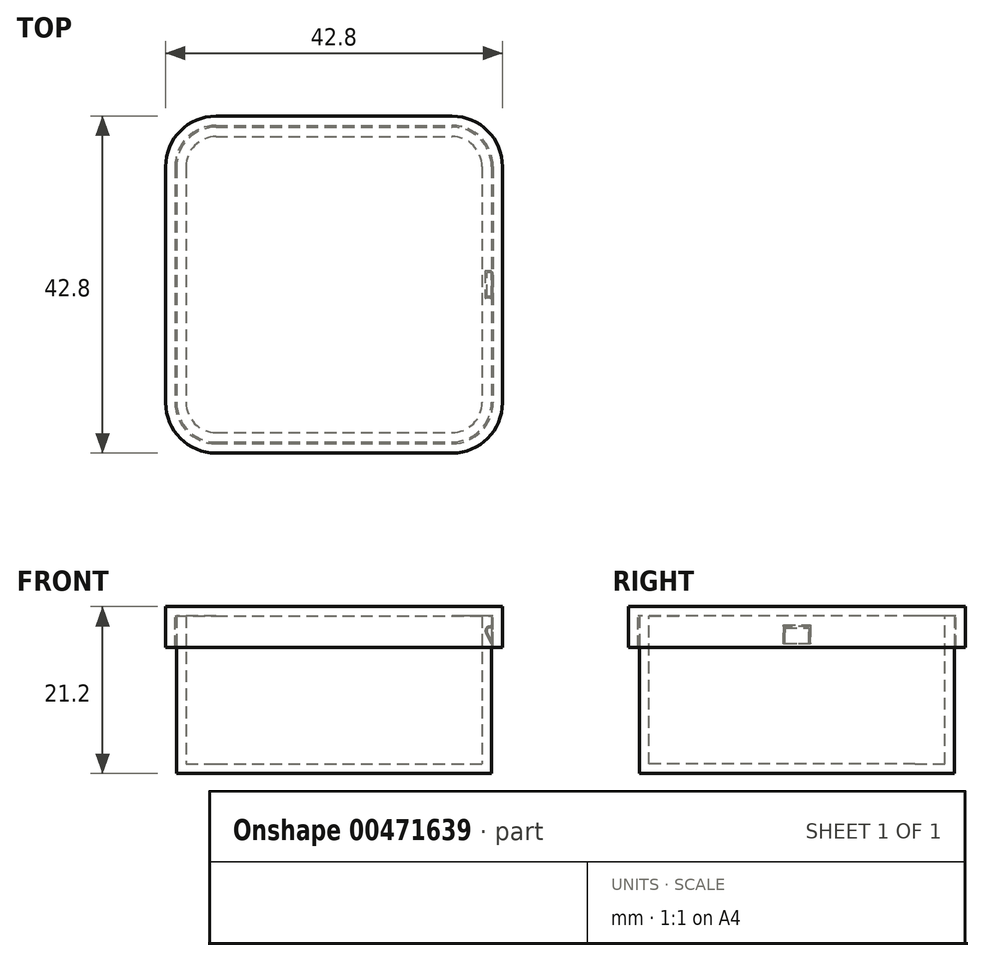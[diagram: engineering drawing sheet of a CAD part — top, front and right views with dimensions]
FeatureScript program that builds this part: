
annotation { "Feature Type Name" : "Feature", "Feature Type Description" : "" }
export const myFeature = defineFeature(function(context is Context, id is Id, definition is map)
    precondition{}
    {
        {
            var Q0;
            Q0=qCreatedBy(makeId("Top.planeOp"),FACE);
            var sketch = newSketch(context, id + "F0", { "sketchPlane" : qUnion([Q0])});
            skLineSegment(sketch, "E0.bottom", {"start": v(-20, 20) * mm, "end": v(20, 20) * mm});
            skLineSegment(sketch, "E0.top", {"start": v(-20, -20) * mm, "end": v(20, -20) * mm});
            skLineSegment(sketch, "E0.left", {"start": v(-20, 20) * mm, "end": v(-20, -20) * mm});
            skLineSegment(sketch, "E0.right", {"start": v(20, 20) * mm, "end": v(20, -20) * mm});
            skPoint(sketch, "E0.middle", {"position": v(0, 0) * mm});
            skSolve(sketch);
        }
        {
            var Q0;
            Q0 = qSketchRegion(id + "F0", true);
            extrude(context, id + "F1", {"entities" : qUnion([Q0]), "depth" : 20 * mm});
        }
        {
            var Q0;
            Q0=makeQuery(id+"F1.opExtrude","SWEPT_EDGE",EDGE,{"disambiguationData":[OSD([sQuery(id+"F0.wireOp",EDGE,"E0.top"),sQuery(id+"F0.wireOp",EDGE,"E0.right")])]});
            var Q1;
            Q1=makeQuery(id+"F1.opExtrude","SWEPT_EDGE",EDGE,{"disambiguationData":[OSD([sQuery(id+"F0.wireOp",EDGE,"E0.bottom"),sQuery(id+"F0.wireOp",EDGE,"E0.right")])]});
            var Q2;
            Q2=makeQuery(id+"F1.opExtrude","SWEPT_EDGE",EDGE,{"disambiguationData":[OSD([sQuery(id+"F0.wireOp",EDGE,"E0.top"),sQuery(id+"F0.wireOp",EDGE,"E0.left")])]});
            var Q3;
            Q3=makeQuery(id+"F1.opExtrude","SWEPT_EDGE",EDGE,{"disambiguationData":[OSD([sQuery(id+"F0.wireOp",EDGE,"E0.bottom"),sQuery(id+"F0.wireOp",EDGE,"E0.left")])]});
            fillet(context, id + "F2", {"entities" : qUnion([Q0, Q1, Q2, Q3]), "radius" : 5 * mm, "tangentPropagation" : true, "allowEdgeOverflow" : false});
        }
        {
            var Q0;
            Q0=makeQuery(id+"F1.opExtrude","CAP_FACE",FACE,{"disambiguationData":[OSD([sQuery(id+"F0.wireOp",EDGE,"E0.bottom"),sQuery(id+"F0.wireOp",EDGE,"E0.top"),sQuery(id+"F0.wireOp",EDGE,"E0.left"),sQuery(id+"F0.wireOp",EDGE,"E0.right")])],"isStart":false});
            shell(context, id + "F3", {"entities" : qUnion([Q0]), "thickness" : 1.2 * mm});
        }
        {
            var Q0;
            Q0=makeQuery(id+"F1.opExtrude","CAP_FACE",FACE,{"disambiguationData":[OSD([sQuery(id+"F0.wireOp",EDGE,"E0.bottom"),sQuery(id+"F0.wireOp",EDGE,"E0.top"),sQuery(id+"F0.wireOp",EDGE,"E0.left"),sQuery(id+"F0.wireOp",EDGE,"E0.right")])],"isStart":false});
            var sketch = newSketch(context, id + "F4", { "sketchPlane" : qUnion([Q0])});
            skLineSegment(sketch, "E1.0", {"start": v(-15, -20) * mm, "end": v(15, -20) * mm});
            skArc(sketch, "E1.1", {"start": v(15, -20) * mm, "mid": v(18.54, -18.54) * mm, "end": v(20, -15) * mm});
            skLineSegment(sketch, "E1.2", {"start": v(20, 15) * mm, "end": v(20, -15) * mm});
            skArc(sketch, "E1.3", {"start": v(20, 15) * mm, "mid": v(18.54, 18.54) * mm, "end": v(15, 20) * mm});
            skLineSegment(sketch, "E1.4", {"start": v(-15, 20) * mm, "end": v(15, 20) * mm});
            skArc(sketch, "E1.5", {"start": v(-15, 20) * mm, "mid": v(-18.54, 18.54) * mm, "end": v(-20, 15) * mm});
            skLineSegment(sketch, "E1.6", {"start": v(-20, 15) * mm, "end": v(-20, -15) * mm});
            skArc(sketch, "E1.7", {"start": v(-20, -15) * mm, "mid": v(-18.54, -18.54) * mm, "end": v(-15, -20) * mm});
            skArc(sketch, "E2.0", {"start": v(-20.2, -15) * mm, "mid": v(-18.68, -18.68) * mm, "end": v(-15, -20.2) * mm});
            skLineSegment(sketch, "E2.1", {"start": v(-20.2, 15) * mm, "end": v(-20.2, -15) * mm});
            skLineSegment(sketch, "E2.2", {"start": v(-15, -20.2) * mm, "end": v(15, -20.2) * mm});
            skArc(sketch, "E2.3", {"start": v(-15, 20.2) * mm, "mid": v(-18.68, 18.68) * mm, "end": v(-20.2, 15) * mm});
            skArc(sketch, "E2.4", {"start": v(15, -20.2) * mm, "mid": v(18.68, -18.68) * mm, "end": v(20.2, -15) * mm});
            skLineSegment(sketch, "E2.5", {"start": v(20.2, 15) * mm, "end": v(20.2, -15) * mm});
            skArc(sketch, "E2.6", {"start": v(20.2, 15) * mm, "mid": v(18.68, 18.68) * mm, "end": v(15, 20.2) * mm});
            skLineSegment(sketch, "E2.7", {"start": v(-15, 20.2) * mm, "end": v(15, 20.2) * mm});
            skArc(sketch, "E3.0", {"start": v(-21.4, -15) * mm, "mid": v(-19.53, -19.53) * mm, "end": v(-15, -21.4) * mm});
            skLineSegment(sketch, "E3.1", {"start": v(-21.4, 15) * mm, "end": v(-21.4, -15) * mm});
            skLineSegment(sketch, "E3.2", {"start": v(-15, -21.4) * mm, "end": v(15, -21.4) * mm});
            skArc(sketch, "E3.3", {"start": v(-15, 21.4) * mm, "mid": v(-19.53, 19.53) * mm, "end": v(-21.4, 15) * mm});
            skArc(sketch, "E3.4", {"start": v(15, -21.4) * mm, "mid": v(19.53, -19.53) * mm, "end": v(21.4, -15) * mm});
            skLineSegment(sketch, "E3.5", {"start": v(21.4, 15) * mm, "end": v(21.4, -15) * mm});
            skArc(sketch, "E3.6", {"start": v(21.4, 15) * mm, "mid": v(19.53, 19.53) * mm, "end": v(15, 21.4) * mm});
            skLineSegment(sketch, "E3.7", {"start": v(-15, 21.4) * mm, "end": v(15, 21.4) * mm});
            skSolve(sketch);
        }
        {
            var Q0;
            Q0=makeQuery(id+"F4.imprint","IMPRINT",FACE,{"disambiguationData":[TD([[makeQuery(id+"F4.imprint","IMPRINT",EDGE,{"derivedFrom":sQuery(id+"F4.wireOp",EDGE,"E2.0")}),-1.0]])]});
            var Q1;
            {var subQ3=sQuery(id+"F0.wireOp",EDGE,"E0.bottom");Q1=makeQuery(id+"F4.imprint","IMPRINT",FACE,{"disambiguationData":[TD([[makeQuery(id+"F4.imprint","IMPRINT",EDGE,{"derivedFrom":makeQuery(id+"F3.opShell","OFFSET_EDGE",EDGE,{"disambiguationData":[OSD([subQ3]),TDD([makeQuery(id+"F1.opExtrude","CAP_EDGE",EDGE,{"disambiguationData":[OSD([subQ3])],"isStart":false})])]})}),-1.0]])]});}
            var Q2;
            Q2=makeQuery(id+"F4.imprint","IMPRINT",FACE,{"disambiguationData":[TD([[makeQuery(id+"F4.imprint","IMPRINT",EDGE,{"derivedFrom":sQuery(id+"F4.wireOp",EDGE,"E1.0")}),1.0]])]});
            var Q3;
            Q3=makeQuery(id+"F4.imprint","IMPRINT",FACE,{"disambiguationData":[TD([[makeQuery(id+"F4.imprint","IMPRINT",EDGE,{"derivedFrom":sQuery(id+"F4.wireOp",EDGE,"E1.0")}),-1.0]])]});
            extrude(context, id + "F5", {"entities" : qUnion([Q0, Q1, Q2, Q3]), "depth" : 1.2 * mm});
        }
        {
            var Q0;
            Q0=makeQuery(id+"F4.imprint","IMPRINT",FACE,{"disambiguationData":[TD([[makeQuery(id+"F4.imprint","IMPRINT",EDGE,{"derivedFrom":sQuery(id+"F4.wireOp",EDGE,"E2.0")}),-1.0]])]});
            extrude(context, id + "F6", {"entities" : qUnion([Q0]), "operationType" : NewBodyOperationType.ADD, "oppositeDirection" : true, "depth" : 4 * mm});
        }
        {
            var Q0;
            Q0=qCreatedBy(makeId("Front.planeOp"),FACE);
            var sketch = newSketch(context, id + "F7", { "sketchPlane" : qUnion([Q0])});
            skLineSegment(sketch, "E4", {"start": v(20.2, 16.5) * mm, "end": v(20.2, 18.5) * mm});
            skLineSegment(sketch, "E5", {"start": v(20.2, 18.5) * mm, "end": v(19.8, 18.5) * mm});
            skLineSegment(sketch, "E6", {"start": v(20.2, 16.5) * mm, "end": v(19.45, 17.91) * mm});
            skArc(sketch, "E7", {"start": v(19.8, 18.5) * mm, "mid": v(19.46, 18.3) * mm, "end": v(19.45, 17.91) * mm});
            skArc(sketch, "E8", {"start": v(19.8, 18.5) * mm, "mid": v(20.08, 18.62) * mm, "end": v(20.2, 18.9) * mm});
            skLineSegment(sketch, "E9", {"start": v(20.2, 18.5) * mm, "end": v(19.4, 18.5) * mm, "construction": true});
            skLineSegment(sketch, "E10", {"start": v(20.2, 18.5) * mm, "end": v(20.2, 18.9) * mm});
            skArc(sketch, "E11.0", {"start": v(19.8, 18.7) * mm, "mid": v(19.92, 18.74) * mm, "end": v(19.99, 18.84) * mm});
            skArc(sketch, "E11.1", {"start": v(19.8, 18.7) * mm, "mid": v(19.29, 18.4) * mm, "end": v(19.27, 17.82) * mm});
            skLineSegment(sketch, "E11.2", {"start": v(20.2, 16.08) * mm, "end": v(19.27, 17.82) * mm});
            skLineSegment(sketch, "E12", {"start": v(19.99, 18.84) * mm, "end": v(20.2, 19.45) * mm});
            skLineSegment(sketch, "E13", {"start": v(20.2, 18.9) * mm, "end": v(20.2, 20) * mm});
            skLineSegment(sketch, "E14", {"start": v(20.2, 16.5) * mm, "end": v(20.2, 16.08) * mm});
            skLineSegment(sketch, "E15.0.1", {"start": v(20.2, 20) * mm, "end": v(20.2, 16) * mm, "construction": true});
            skLineSegment(sketch, "E15.0.3", {"start": v(20.2, 16) * mm, "end": v(20.2, 20) * mm, "construction": true});
            skLineSegment(sketch, "E16.0", {"start": v(20, 20) * mm, "end": v(20, 0) * mm, "construction": true});
            skSolve(sketch);
        }
        {
            var Q0;
            Q0=makeQuery(id+"F7.imprint","IMPRINT",FACE,{"disambiguationData":[TD([[makeQuery(id+"F7.imprint","IMPRINT",EDGE,{"derivedFrom":sQuery(id+"F7.wireOp",EDGE,"E4")}),1.0]])]});
            var Q1;
            Q1=makeQuery(id+"F7.imprint","IMPRINT",FACE,{"disambiguationData":[TD([[makeQuery(id+"F7.imprint","IMPRINT",EDGE,{"derivedFrom":sQuery(id+"F7.wireOp",EDGE,"E5")}),-1.0]])]});
            var Q2;
            Q2=makeQuery(id+"F7.imprint","IMPRINT",FACE,{"disambiguationData":[TD([[makeQuery(id+"F7.imprint","IMPRINT",EDGE,{"derivedFrom":sQuery(id+"F7.wireOp",EDGE,"E6")}),1.0]])]});
            extrude(context, id + "F8", {"entities" : qUnion([Q0, Q1, Q2]), "operationType" : NewBodyOperationType.REMOVE, "endBound" : BoundingType.SYMMETRIC, "oppositeDirection" : true, "depth" : 3.4 * mm});
        }
        {
            var Q0;
            Q0=makeQuery(id+"F7.imprint","IMPRINT",FACE,{"disambiguationData":[TD([[makeQuery(id+"F7.imprint","IMPRINT",EDGE,{"derivedFrom":sQuery(id+"F7.wireOp",EDGE,"E4")}),1.0]])]});
            extrude(context, id + "F9", {"entities" : qUnion([Q0]), "operationType" : NewBodyOperationType.ADD, "endBound" : BoundingType.SYMMETRIC, "depth" : 3 * mm});
        }
        {
            var Q0;
            Q0=makeQuery(id+"F5.opExtrude","CAP_FACE",FACE,{"disambiguationData":[OSD([sQuery(id+"F4.wireOp",EDGE,"E3.0"),sQuery(id+"F4.wireOp",EDGE,"E3.1"),sQuery(id+"F4.wireOp",EDGE,"E3.2"),sQuery(id+"F4.wireOp",EDGE,"E3.3"),sQuery(id+"F4.wireOp",EDGE,"E3.4"),sQuery(id+"F4.wireOp",EDGE,"E3.5"),sQuery(id+"F4.wireOp",EDGE,"E3.6"),sQuery(id+"F4.wireOp",EDGE,"E3.7")])],"isStart":false});
            var sketch = newSketch(context, id + "F10", { "sketchPlane" : qUnion([Q0])});
            skCircle(sketch, "E17", {"center": v(0, 0) * mm, "radius": 21.4 * mm, "construction": true});
            skSolve(sketch);
        }
    });
